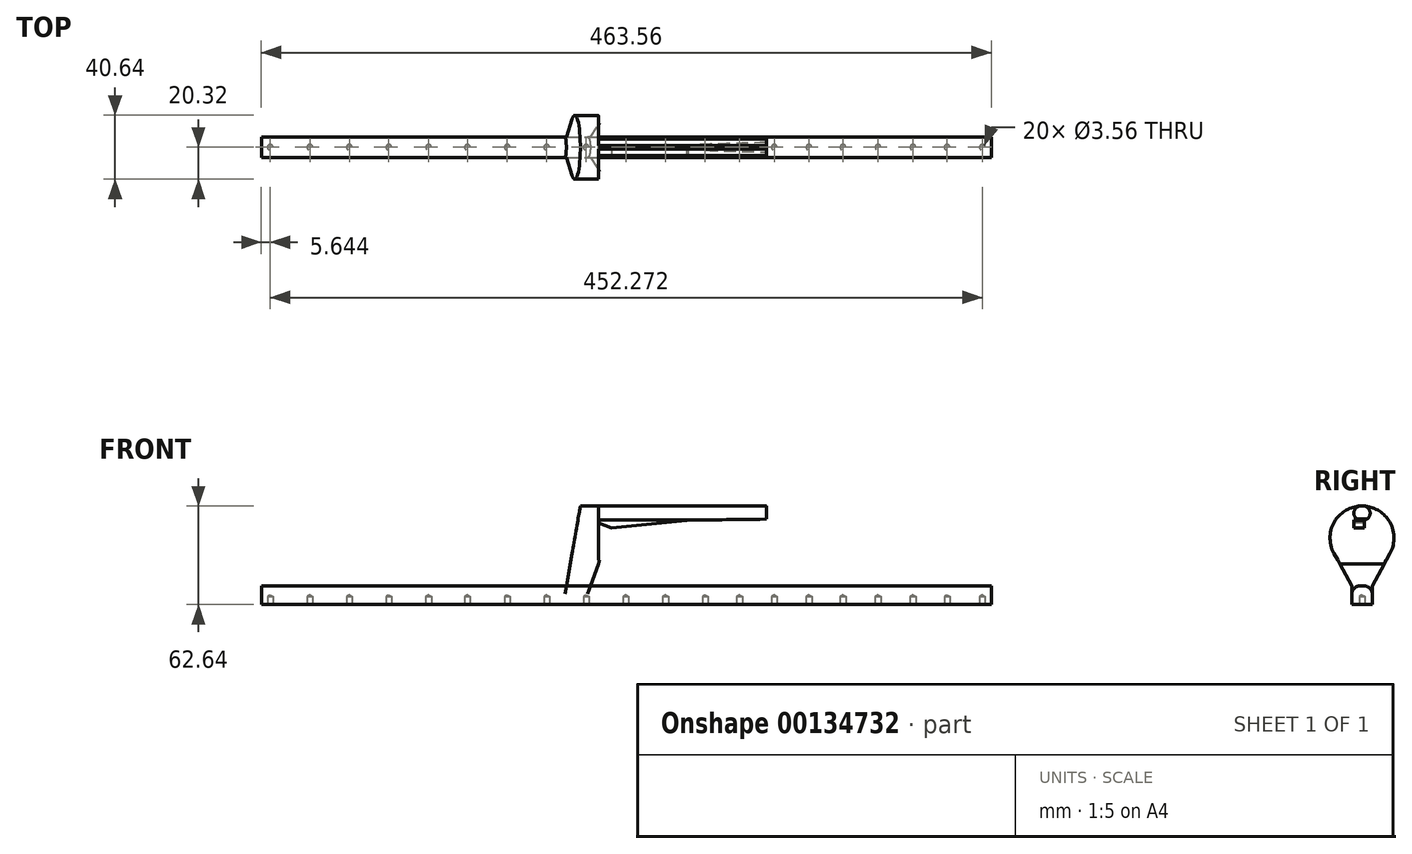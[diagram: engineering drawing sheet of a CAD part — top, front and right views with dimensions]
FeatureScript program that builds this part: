
annotation { "Feature Type Name" : "Feature", "Feature Type Description" : "" }
export const myFeature = defineFeature(function(context is Context, id is Id, definition is map)
    precondition{}
    {
        {
            var Q0;
            Q0=qCreatedBy(makeId("Front.planeOp"),FACE);
            var sketch = newSketch(context, id + "F0", { "sketchPlane" : qUnion([Q0])});
            skLineSegment(sketch, "E0.bottom", {"start": v(-231.77, 0) * mm, "end": v(231.77, 0) * mm});
            skLineSegment(sketch, "E0.top", {"start": v(-231.78, 11.84) * mm, "end": v(231.78, 11.84) * mm});
            skLineSegment(sketch, "E0.left", {"start": v(-231.78, 0) * mm, "end": v(-231.78, 11.84) * mm});
            skLineSegment(sketch, "E0.right", {"start": v(231.78, 0) * mm, "end": v(231.78, 11.84) * mm});
            skSolve(sketch);
        }
        {
            var Q0;
            Q0 = qSketchRegion(id + "F0", true);
            extrude(context, id + "F1", {"entities" : qUnion([Q0]), "depth" : 6.48 * mm, "hasSecondDirection" : true, "secondDirectionOppositeDirection" : true, "secondDirectionDepth" : 6.48 * mm});
        }
        {
            var Q0;
            Q0=qCreatedBy(makeId("Right.planeOp"),FACE);
            cPlane(context, id + "F2", {"entities" : qUnion([Q0]), "cplaneType" : CPlaneType.OFFSET, "offset" : 38.1 * mm, "oppositeDirection" : true, "width" : 152.4 * mm, "height" : 152.4 * mm});
        }
        {
            var Q0;
            Q0=qCreatedBy(id+"F2.planeOp",FACE);
            var sketch = newSketch(context, id + "F3", { "sketchPlane" : qUnion([Q0])});
            skLineSegment(sketch, "E1", {"start": v(6.48, 0) * mm, "end": v(-6.48, 0) * mm, "construction": true});
            skLineSegment(sketch, "E2", {"start": v(-6.48, 0) * mm, "end": v(-6.48, 11.84) * mm, "construction": true});
            skLineSegment(sketch, "E3", {"start": v(-6.48, 11.84) * mm, "end": v(6.48, 11.84) * mm, "construction": true});
            skLineSegment(sketch, "E4", {"start": v(6.48, 11.84) * mm, "end": v(6.48, 0) * mm, "construction": true});
            skLineSegment(sketch, "E5", {"start": v(0, 0) * mm, "end": v(-17.82, 32.57) * mm});
            skLineSegment(sketch, "E6", {"start": v(0, 0) * mm, "end": v(17.82, 32.57) * mm});
            skLineSegment(sketch, "E7", {"start": v(0, 0) * mm, "end": v(0, 62.64) * mm, "construction": true});
            skPoint(sketch, "E7.endSnap0", {"position": v(0, 11.84) * mm});
            skArc(sketch, "E8", {"start": v(17.82, 32.57) * mm, "mid": v(0, 62.64) * mm, "end": v(-17.82, 32.57) * mm});
            skSolve(sketch);
        }
        {
            var Q0;
            Q0 = qSketchRegion(id + "F3", true);
            extrude(context, id + "F4", {"entities" : qUnion([Q0]), "operationType" : NewBodyOperationType.ADD, "depth" : 127 * mm});
        }
        {
            var Q0;
            Q0=qCreatedBy(makeId("Front.planeOp"),FACE);
            var sketch = newSketch(context, id + "F5", { "sketchPlane" : qUnion([Q0])});
            skLineSegment(sketch, "E9", {"start": v(0, 0) * mm, "end": v(-38.1, 0) * mm, "construction": true});
            skLineSegment(sketch, "E10", {"start": v(-38.1, 0) * mm, "end": v(-38.1, 11.84) * mm, "construction": true});
            skLineSegment(sketch, "E11", {"start": v(-38.1, 11.84) * mm, "end": v(-29.14, 62.64) * mm});
            skLineSegment(sketch, "E12", {"start": v(-29.14, 62.64) * mm, "end": v(-38.1, 62.64) * mm});
            skLineSegment(sketch, "E13", {"start": v(-38.1, 11.84) * mm, "end": v(-22.86, 11.84) * mm, "construction": true});
            skLineSegment(sketch, "E14", {"start": v(-22.86, 11.84) * mm, "end": v(-9.4, 48.83) * mm});
            skLineSegment(sketch, "E15", {"start": v(88.9, 62.64) * mm, "end": v(88.9, 54.25) * mm, "construction": true});
            skLineSegment(sketch, "E16", {"start": v(88.9, 58.45) * mm, "end": v(38.1, 58.45) * mm, "construction": true});
            skLineSegment(sketch, "E17", {"start": v(88.9, 54.25) * mm, "end": v(38.1, 53.6) * mm});
            skLineSegment(sketch, "E18", {"start": v(38.1, 53.6) * mm, "end": v(-9.4, 48.83) * mm});
            skLineSegment(sketch, "E19", {"start": v(-38.1, 11.84) * mm, "end": v(88.9, 11.84) * mm, "construction": true});
            skPoint(sketch, "E19.endSnap0", {"position": v(-30.48, 11.84) * mm});
            skLineSegment(sketch, "E20", {"start": v(88.9, 11.84) * mm, "end": v(88.9, 54.25) * mm, "construction": true});
            skLineSegment(sketch, "E21", {"start": v(88.9, 54.25) * mm, "end": v(88.9, 11.84) * mm});
            skLineSegment(sketch, "E22", {"start": v(-38.1, 62.64) * mm, "end": v(-38.1, 11.84) * mm});
            skLineSegment(sketch, "E23", {"start": v(-22.86, 11.84) * mm, "end": v(88.9, 11.84) * mm});
            skSolve(sketch);
        }
        {
            var Q0;
            Q0 = qSketchRegion(id + "F5", true);
            extrude(context, id + "F6", {"entities" : qUnion([Q0]), "operationType" : NewBodyOperationType.REMOVE, "endBound" : BoundingType.THROUGH_ALL, "oppositeDirection" : true, "depth" : 25.4 * mm, "hasSecondDirection" : true, "secondDirectionBound" : SecondDirectionBoundingType.THROUGH_ALL, "secondDirectionOppositeDirection" : false, "secondDirectionDepth" : 25.4 * mm});
        }
        {
            var Q0;
            Q0=makeQuery(id+"F4.opExtrude","CAP_FACE",FACE,{"disambiguationData":[OSD([sQuery(id+"F3.wireOp",EDGE,"E5"),sQuery(id+"F3.wireOp",EDGE,"E6"),sQuery(id+"F3.wireOp",EDGE,"E8")])],"isStart":false});
            var sketch = newSketch(context, id + "F7", { "sketchPlane" : qUnion([Q0])});
            skArc(sketch, "E24", {"start": v(-0.76, 62.62) * mm, "mid": v(0, 22) * mm, "end": v(0.76, 62.62) * mm});
            skLineSegment(sketch, "E25", {"start": v(-16.88, 53.62) * mm, "end": v(-0.67, 53.62) * mm});
            skArc(sketch, "E26", {"start": v(-0.76, 62.62) * mm, "mid": v(-5.17, 58.08) * mm, "end": v(-0.67, 53.62) * mm});
            skArc(sketch, "E27", {"start": v(0.67, 53.62) * mm, "mid": v(5.17, 58.08) * mm, "end": v(0.76, 62.62) * mm});
            skLineSegment(sketch, "E28.trimOffspring", {"start": v(0.67, 53.62) * mm, "end": v(16.88, 53.62) * mm});
            skPoint(sketch, "E29.start.orphan", {"position": v(0, 53.62) * mm});
            skPoint(sketch, "E30.start.orphan", {"position": v(0, 62.64) * mm});
            skSolve(sketch);
        }
        {
            var Q0;
            Q0 = qSketchRegion(id + "F7", true);
            extrude(context, id + "F8", {"entities" : qUnion([Q0]), "operationType" : NewBodyOperationType.REMOVE, "oppositeDirection" : true, "depth" : 106.68 * mm});
        }
        {
            var Q0;
            {var subQ0=sQuery(id+"F3.wireOp",EDGE,"E5");var subQ1=sQuery(id+"F0.wireOp",EDGE,"E0.left");var subQ2=sQuery(id+"F0.wireOp",EDGE,"E0.top");Q0=makeQuery(id+"F4.boolean.opBoolean","SPLIT",EDGE,{"disambiguationData":[TD([makeQuery(id+"F1.opExtrude","CAP_FACE",FACE,{"disambiguationData":[OSD([sQuery(id+"F0.wireOp",EDGE,"E0.bottom"),subQ2,subQ1,sQuery(id+"F0.wireOp",EDGE,"E0.right")])],"isStart":false}),makeQuery(id+"F1.opExtrude","SWEPT_FACE",FACE,{"disambiguationData":[OSD([subQ2])]}),makeQuery(id+"F1.opExtrude","SWEPT_FACE",FACE,{"disambiguationData":[OSD([subQ1])]}),makeQuery(id+"F4.opExtrude","SWEPT_FACE",FACE,{"disambiguationData":[OSD([subQ0])]}),makeQuery(id+"F4.opExtrude","CAP_FACE",FACE,{"disambiguationData":[OSD([subQ0,sQuery(id+"F3.wireOp",EDGE,"E6"),sQuery(id+"F3.wireOp",EDGE,"E8")])],"isStart":true})])],"derivedFrom":makeQuery(id+"F1.opExtrude","CAP_EDGE",EDGE,{"disambiguationData":[OSD([subQ2])],"isStart":false})});}
            var Q1;
            {var subQ0=sQuery(id+"F3.wireOp",EDGE,"E6");var subQ1=sQuery(id+"F0.wireOp",EDGE,"E0.left");var subQ2=sQuery(id+"F0.wireOp",EDGE,"E0.top");Q1=makeQuery(id+"F4.boolean.opBoolean","SPLIT",EDGE,{"disambiguationData":[TD([makeQuery(id+"F1.opExtrude","CAP_FACE",FACE,{"disambiguationData":[OSD([sQuery(id+"F0.wireOp",EDGE,"E0.bottom"),subQ2,subQ1,sQuery(id+"F0.wireOp",EDGE,"E0.right")])],"isStart":true}),makeQuery(id+"F1.opExtrude","SWEPT_FACE",FACE,{"disambiguationData":[OSD([subQ2])]}),makeQuery(id+"F1.opExtrude","SWEPT_FACE",FACE,{"disambiguationData":[OSD([subQ1])]}),makeQuery(id+"F4.opExtrude","CAP_FACE",FACE,{"disambiguationData":[OSD([sQuery(id+"F3.wireOp",EDGE,"E5"),subQ0,sQuery(id+"F3.wireOp",EDGE,"E8")])],"isStart":true}),makeQuery(id+"F4.opExtrude","SWEPT_FACE",FACE,{"disambiguationData":[OSD([subQ0])]})])],"derivedFrom":makeQuery(id+"F1.opExtrude","CAP_EDGE",EDGE,{"disambiguationData":[OSD([subQ2])],"isStart":true})});}
            var Q2;
            {var subQ0=sQuery(id+"F3.wireOp",EDGE,"E8");var subQ1=sQuery(id+"F3.wireOp",EDGE,"E6");var subQ2=sQuery(id+"F3.wireOp",EDGE,"E5");var subQ3=sQuery(id+"F0.wireOp",EDGE,"E0.right");var subQ4=sQuery(id+"F0.wireOp",EDGE,"E0.top");var subQ5=makeQuery(id+"F1.opExtrude","CAP_FACE",FACE,{"disambiguationData":[OSD([sQuery(id+"F0.wireOp",EDGE,"E0.bottom"),subQ4,sQuery(id+"F0.wireOp",EDGE,"E0.left"),subQ3])],"isStart":false});var subQ6=makeQuery(id+"F4.opExtrude","SWEPT_FACE",FACE,{"disambiguationData":[OSD([subQ2])]});var subQ7=makeQuery(id+"F1.opExtrude","SWEPT_FACE",FACE,{"disambiguationData":[OSD([subQ4])]});var subQ8=makeQuery(id+"F4.opExtrude","CAP_FACE",FACE,{"disambiguationData":[OSD([subQ2,subQ1,subQ0])],"isStart":false});var subQ9=makeQuery(id+"F1.opExtrude","CAP_EDGE",EDGE,{"disambiguationData":[OSD([subQ4])],"isStart":false});Q2=makeQuery(id+"F6.boolean.opBoolean","MERGE",EDGE,{"derivedFrom":[makeQuery(id+"F4.boolean.opBoolean","SPLIT",EDGE,{"disambiguationData":[TD([subQ5,subQ7,makeQuery(id+"F1.opExtrude","SWEPT_FACE",FACE,{"disambiguationData":[OSD([subQ3])]}),subQ6,subQ8])],"derivedFrom":subQ9}),makeQuery(id+"F4.boolean.opBoolean","SPLIT",EDGE,{"disambiguationData":[TD([subQ5,subQ7,subQ6,makeQuery(id+"F4.opExtrude","CAP_FACE",FACE,{"disambiguationData":[OSD([subQ2,subQ1,subQ0])],"isStart":true}),subQ8])],"derivedFrom":subQ9})]});}
            var Q3;
            {var subQ0=sQuery(id+"F3.wireOp",EDGE,"E8");var subQ1=sQuery(id+"F3.wireOp",EDGE,"E6");var subQ2=sQuery(id+"F3.wireOp",EDGE,"E5");var subQ3=makeQuery(id+"F4.opExtrude","CAP_FACE",FACE,{"disambiguationData":[OSD([subQ2,subQ1,subQ0])],"isStart":false});var subQ4=sQuery(id+"F0.wireOp",EDGE,"E0.top");var subQ5=makeQuery(id+"F1.opExtrude","SWEPT_FACE",FACE,{"disambiguationData":[OSD([subQ4])]});var subQ6=sQuery(id+"F0.wireOp",EDGE,"E0.right");var subQ7=makeQuery(id+"F1.opExtrude","CAP_FACE",FACE,{"disambiguationData":[OSD([sQuery(id+"F0.wireOp",EDGE,"E0.bottom"),subQ4,sQuery(id+"F0.wireOp",EDGE,"E0.left"),subQ6])],"isStart":true});var subQ8=makeQuery(id+"F4.opExtrude","SWEPT_FACE",FACE,{"disambiguationData":[OSD([subQ1])]});var subQ9=makeQuery(id+"F1.opExtrude","CAP_EDGE",EDGE,{"disambiguationData":[OSD([subQ4])],"isStart":true});Q3=makeQuery(id+"F6.boolean.opBoolean","MERGE",EDGE,{"derivedFrom":[makeQuery(id+"F4.boolean.opBoolean","SPLIT",EDGE,{"disambiguationData":[TD([subQ7,subQ5,makeQuery(id+"F1.opExtrude","SWEPT_FACE",FACE,{"disambiguationData":[OSD([subQ6])]}),subQ3,subQ8])],"derivedFrom":subQ9}),makeQuery(id+"F4.boolean.opBoolean","SPLIT",EDGE,{"disambiguationData":[TD([subQ7,subQ5,makeQuery(id+"F4.opExtrude","CAP_FACE",FACE,{"disambiguationData":[OSD([subQ2,subQ1,subQ0])],"isStart":true}),subQ3,subQ8])],"derivedFrom":subQ9})]});}
            fillet(context, id + "F9", {"entities" : qUnion([Q0, Q1, Q2, Q3]), "radius" : 5.08 * mm, "tangentPropagation" : true, "allowEdgeOverflow" : false});
        }
        {
            var Q0;
            Q0=makeQuery(id+"F1.opExtrude","SWEPT_FACE",FACE,{"disambiguationData":[OSD([sQuery(id+"F0.wireOp",EDGE,"E0.bottom")])]});
            var sketch = newSketch(context, id + "F10", { "sketchPlane" : qUnion([Q0])});
            skPoint(sketch, "E31", {"position": v(24.94, 0) * mm});
            skPoint(sketch, "E32", {"position": v(50.16, 0) * mm});
            skPoint(sketch, "E33", {"position": v(71.9, 0) * mm});
            skPoint(sketch, "E34", {"position": v(93.98, 0) * mm});
            skPoint(sketch, "E35", {"position": v(116.02, 0) * mm});
            skPoint(sketch, "E36", {"position": v(137.64, 0) * mm});
            skPoint(sketch, "E37", {"position": v(159.9, 0) * mm});
            skPoint(sketch, "E38", {"position": v(182.07, 0) * mm});
            skPoint(sketch, "E39", {"position": v(203.78, 0) * mm});
            skPoint(sketch, "E40", {"position": v(226.14, 0) * mm});
            skPoint(sketch, "E41", {"position": v(-0.2, 0) * mm});
            skPoint(sketch, "E42", {"position": v(-25.48, 0) * mm});
            skPoint(sketch, "E43", {"position": v(-150.83, 0) * mm});
            skPoint(sketch, "E44", {"position": v(-50.58, 0) * mm});
            skPoint(sketch, "E45", {"position": v(-226.14, 0) * mm});
            skPoint(sketch, "E46", {"position": v(-75.58, 0) * mm});
            skPoint(sketch, "E47", {"position": v(-200.94, 0) * mm});
            skPoint(sketch, "E48", {"position": v(-100.87, 0) * mm});
            skPoint(sketch, "E49", {"position": v(-175.88, 0) * mm});
            skPoint(sketch, "E50", {"position": v(-125.53, 0) * mm});
            skLineSegment(sketch, "E51.0", {"start": v(231.77, 6.93) * mm, "end": v(231.77, -6.02) * mm, "construction": true});
            skLineSegment(sketch, "E52.0", {"start": v(231.77, 6.48) * mm, "end": v(231.77, -6.48) * mm, "construction": true});
            skLineSegment(sketch, "E53.0", {"start": v(-231.77, 6.48) * mm, "end": v(231.77, 6.48) * mm, "construction": true});
            skLineSegment(sketch, "E54.0", {"start": v(-231.77, -6.48) * mm, "end": v(231.77, -6.48) * mm, "construction": true});
            skSolve(sketch);
        }
        {
            var Q0;
            Q0=sQuery(id+"F10.wireOp",VERTEX,"E45");
            var Q1;
            Q1=sQuery(id+"F10.wireOp",VERTEX,"E47");
            var Q2;
            Q2=sQuery(id+"F10.wireOp",VERTEX,"E49");
            var Q3;
            Q3=sQuery(id+"F10.wireOp",VERTEX,"E43");
            var Q4;
            Q4=sQuery(id+"F10.wireOp",VERTEX,"E50");
            var Q5;
            Q5=sQuery(id+"F10.wireOp",VERTEX,"E48");
            var Q6;
            Q6=sQuery(id+"F10.wireOp",VERTEX,"E46");
            var Q7;
            Q7=sQuery(id+"F10.wireOp",VERTEX,"E44");
            var Q8;
            Q8=sQuery(id+"F10.wireOp",VERTEX,"E42");
            var Q9;
            Q9=sQuery(id+"F10.wireOp",VERTEX,"E41");
            var Q10;
            Q10=sQuery(id+"F10.wireOp",VERTEX,"E31");
            var Q11;
            Q11=sQuery(id+"F10.wireOp",VERTEX,"E32");
            var Q12;
            Q12=sQuery(id+"F10.wireOp",VERTEX,"E33");
            var Q13;
            Q13=sQuery(id+"F10.wireOp",VERTEX,"E34");
            var Q14;
            Q14=sQuery(id+"F10.wireOp",VERTEX,"E35");
            var Q15;
            Q15=sQuery(id+"F10.wireOp",VERTEX,"E36");
            var Q16;
            Q16=sQuery(id+"F10.wireOp",VERTEX,"E37");
            var Q17;
            Q17=sQuery(id+"F10.wireOp",VERTEX,"E38");
            var Q18;
            Q18=sQuery(id+"F10.wireOp",VERTEX,"E39");
            var Q19;
            Q19=sQuery(id+"F10.wireOp",VERTEX,"E40");
            var Q20;
            Q20=makeQuery(id+"F1.opExtrude","SWEPT_BODY",BODY,{"disambiguationData":[OSD([sQuery(id+"F0.wireOp",EDGE,"E0.bottom"),sQuery(id+"F0.wireOp",EDGE,"E0.top"),sQuery(id+"F0.wireOp",EDGE,"E0.left"),sQuery(id+"F0.wireOp",EDGE,"E0.right")])]});
            hole(context, id + "F11", {"style" : HoleStyle.SIMPLE, "endStyle" : HoleEndStyle.BLIND, "holeDiameter" : 3.56 * mm, "majorDiameter" : 6.35 * mm, "holeDepth" : 5.08 * mm, "locations" : qUnion([Q0, Q1, Q2, Q3, Q4, Q5, Q6, Q7, Q8, Q9, Q10, Q11, Q12, Q13, Q14, Q15, Q16, Q17, Q18, Q19]), "scope" : qUnion([Q20]), "tappedDepth" : 12.7 * mm, "tapClearance" : 3});
        }
        {
            var Q0;
            Q0=makeQuery(id+"F8.boolean.opBoolean","COPY",FACE,{"derivedFrom":makeQuery(id+"F8.opExtrude","SWEPT_FACE",FACE,{"disambiguationData":[OSD([sQuery(id+"F7.wireOp",EDGE,"E25")])]})});
            var sketch = newSketch(context, id + "F12", { "sketchPlane" : qUnion([Q0])});
            skLineSegment(sketch, "E55", {"start": v(88.91, 5.18) * mm, "end": v(-17.77, 5.18) * mm, "construction": true});
            skLineSegment(sketch, "E56", {"start": v(-17.77, 5.18) * mm, "end": v(-17.77, 16.87) * mm, "construction": true});
            skLineSegment(sketch, "E57", {"start": v(-17.77, 16.87) * mm, "end": v(39.23, 16.87) * mm, "construction": true});
            skLineSegment(sketch, "E58", {"start": v(39.23, 16.87) * mm, "end": v(39.23, 5.18) * mm, "construction": true});
            skLineSegment(sketch, "E59.bottom", {"start": v(-17.77, 5.18) * mm, "end": v(39.28, 5.18) * mm});
            skLineSegment(sketch, "E59.top", {"start": v(-17.77, 29.45) * mm, "end": v(39.28, 29.45) * mm});
            skLineSegment(sketch, "E59.left", {"start": v(-17.77, 5.18) * mm, "end": v(-17.77, 29.45) * mm});
            skLineSegment(sketch, "E59.right", {"start": v(39.28, 5.18) * mm, "end": v(39.28, 29.45) * mm});
            skLineSegment(sketch, "E60.MirrorCS", {"start": v(-17.77, -29.45) * mm, "end": v(39.28, -29.45) * mm});
            skLineSegment(sketch, "E61.MirrorCS", {"start": v(39.28, -5.18) * mm, "end": v(39.28, -29.45) * mm});
            skLineSegment(sketch, "E62.MirrorCS", {"start": v(-17.77, -5.18) * mm, "end": v(-17.77, -29.45) * mm});
            skLineSegment(sketch, "E63.MirrorCS", {"start": v(88.91, -5.18) * mm, "end": v(-17.77, -5.18) * mm, "construction": true});
            skLineSegment(sketch, "E64", {"start": v(-17.77, -5.18) * mm, "end": v(39.28, -5.18) * mm});
            skSolve(sketch);
        }
        {
            var Q0;
            Q0 = qSketchRegion(id + "F12", true);
            extrude(context, id + "F13", {"entities" : qUnion([Q0]), "operationType" : NewBodyOperationType.REMOVE, "oppositeDirection" : true, "depth" : 25.4 * mm});
        }
        {
            var Q0;
            Q0=makeQuery(id+"F13.boolean.opBoolean","COPY",FACE,{"derivedFrom":makeQuery(id+"F13.opExtrude","SWEPT_FACE",FACE,{"disambiguationData":[OSD([sQuery(id+"F12.wireOp",EDGE,"E59.bottom")])]})});
            extrude(context, id + "F14", {"entities" : qUnion([Q0]), "operationType" : NewBodyOperationType.REMOVE, "oppositeDirection" : true, "depth" : 3.8 * mm});
        }
        {
            var Q0;
            Q0=makeQuery(id+"F6.boolean.opBoolean","COPY",FACE,{"derivedFrom":makeQuery(id+"F6.opExtrude","SWEPT_FACE",FACE,{"disambiguationData":[OSD([sQuery(id+"F5.wireOp",EDGE,"E14")])]})});
            var Q1;
            {var subQ0=sQuery(id+"F12.wireOp",EDGE,"E62.MirrorCS");Q1=makeQuery(id+"FAA1q4XDeRfOqSx_1.boolean.opBoolean","MERGE",FACE,{"derivedFrom":[makeQuery(id+"F13.boolean.opBoolean","COPY",FACE,{"derivedFrom":makeQuery(id+"F13.opExtrude","SWEPT_FACE",FACE,{"disambiguationData":[OSD([subQ0])]})}),makeQuery(id+"FAA1q4XDeRfOqSx_1.opExtrude","SWEPT_FACE",FACE,{"disambiguationData":[OSD([subQ0,sQuery(id+"F12.wireOp",EDGE,"E64")])]})]});}
            extrude(context, id + "F15", {"entities" : qUnion([Q0]), "operationType" : NewBodyOperationType.REMOVE, "endBound" : BoundingType.UP_TO_SURFACE, "oppositeDirection" : true, "endBoundEntityFace" : qUnion([Q1]), "depth" : 25.4 * mm});
        }
    });
